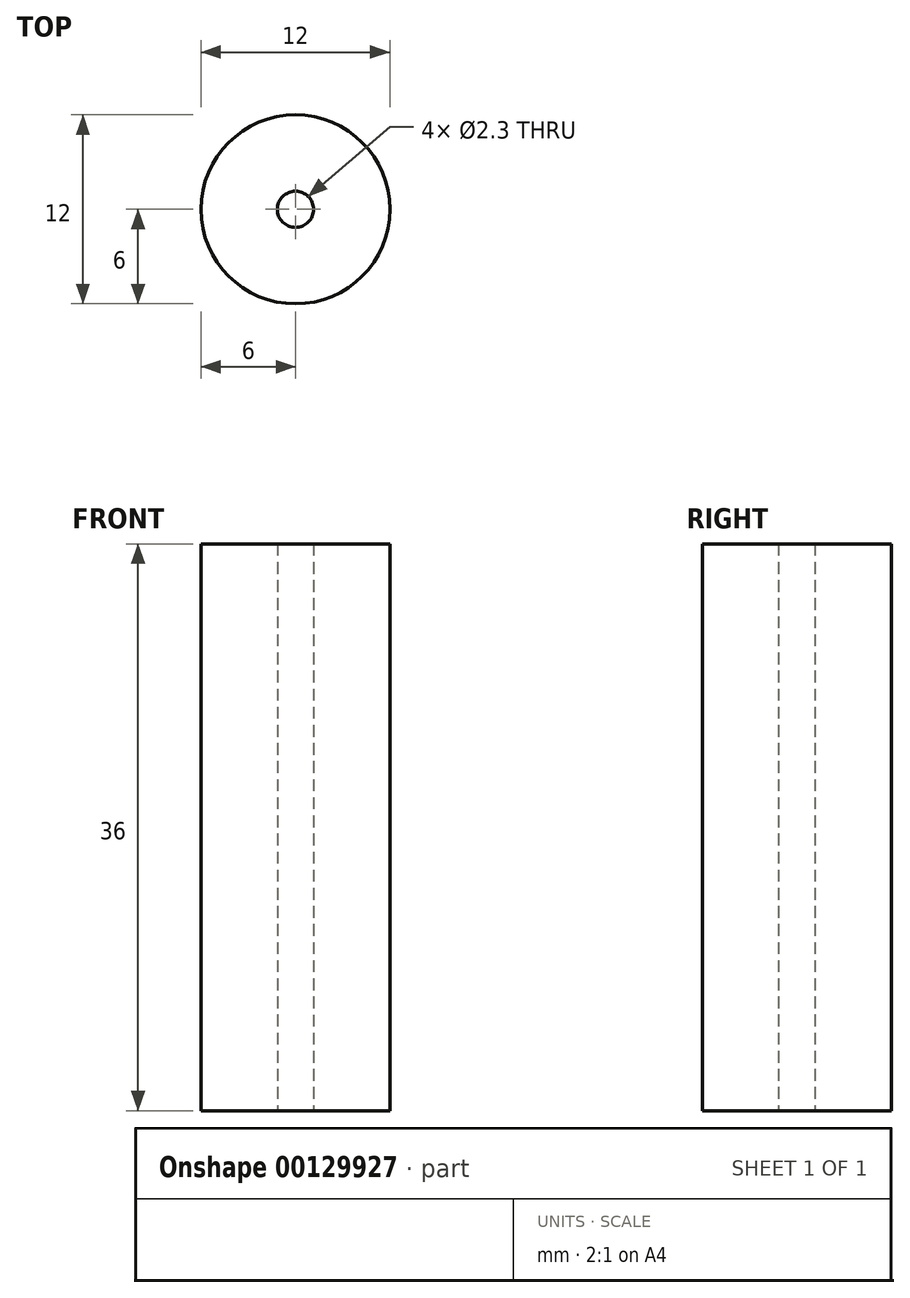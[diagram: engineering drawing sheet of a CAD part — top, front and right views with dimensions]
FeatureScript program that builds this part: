
annotation { "Feature Type Name" : "Feature", "Feature Type Description" : "" }
export const myFeature = defineFeature(function(context is Context, id is Id, definition is map)
    precondition{}
    {
        {
            var Q0;
            Q0=qCreatedBy(makeId("Top.planeOp"),FACE);
            var sketch = newSketch(context, id + "F0", { "sketchPlane" : qUnion([Q0])});
            skCircle(sketch, "E0", {"center": v(0, 0) * mm, "radius": 1.15 * mm});
            skCircle(sketch, "E1", {"center": v(0, 0) * mm, "radius": 6 * mm});
            skSolve(sketch);
        }
        {
            var Q0;
            Q0=makeQuery(id+"F0.imprint","IMPRINT",FACE,{"disambiguationData":[TD([[makeQuery(id+"F0.imprint","IMPRINT",EDGE,{"derivedFrom":sQuery(id+"F0.wireOp",EDGE,"E0")}),-1.0]])]});
            extrude(context, id + "F1", {"entities" : qUnion([Q0]), "depth" : 36 * mm});
        }
    });
